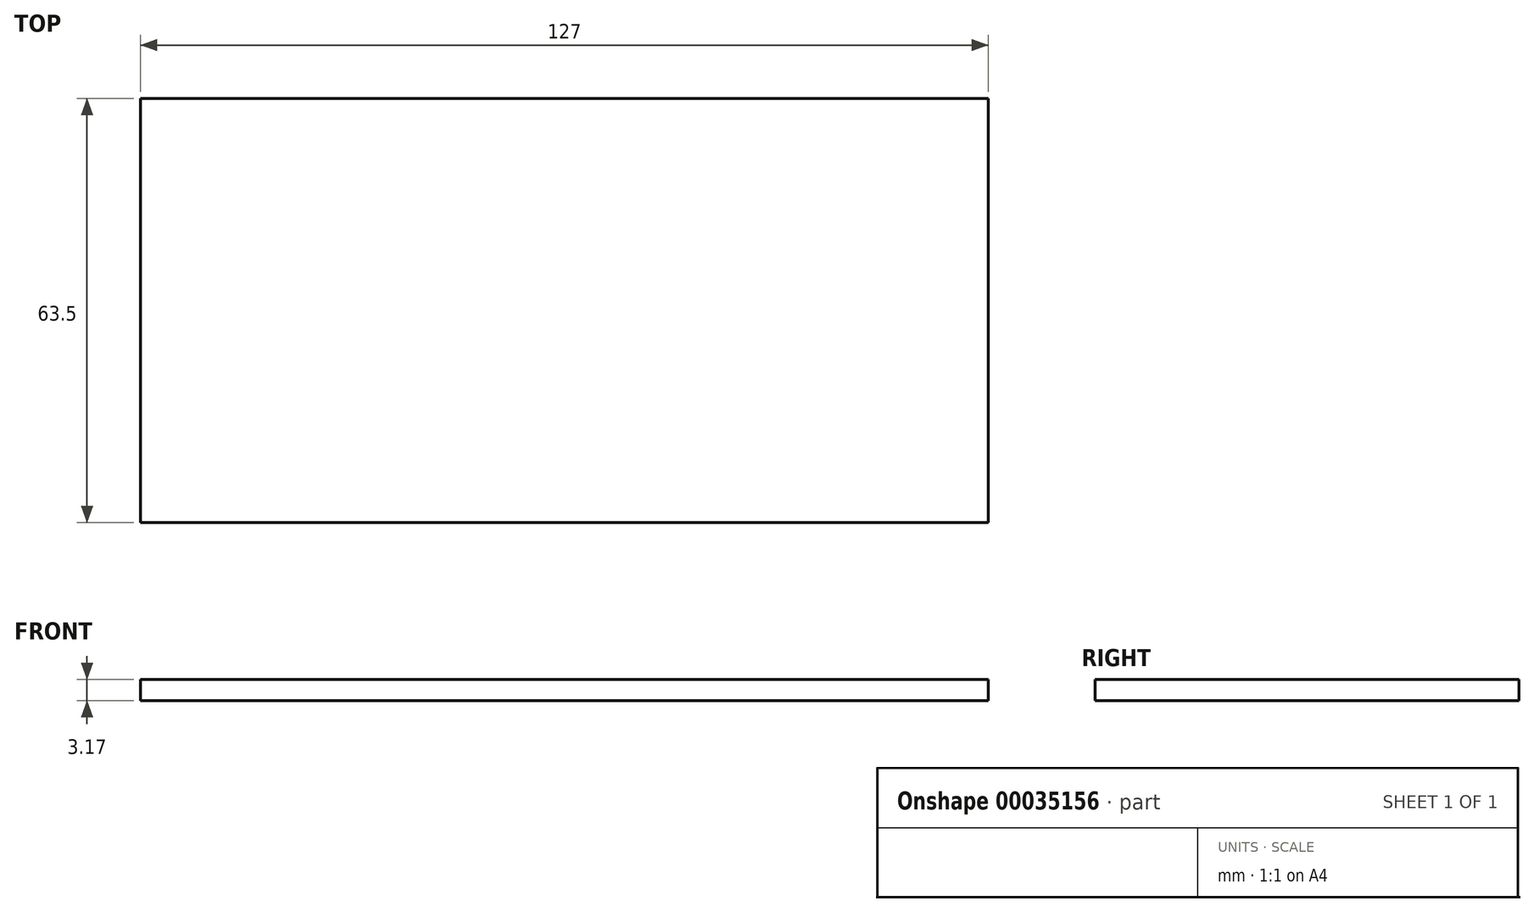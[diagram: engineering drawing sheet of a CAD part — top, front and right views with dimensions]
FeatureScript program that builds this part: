
annotation { "Feature Type Name" : "Feature", "Feature Type Description" : "" }
export const myFeature = defineFeature(function(context is Context, id is Id, definition is map)
    precondition{}
    {
        {
            var Q0;
            Q0=qCreatedBy(makeId("Top.planeOp"),FACE);
            var sketch = newSketch(context, id + "F0", { "sketchPlane" : qUnion([Q0])});
            skLineSegment(sketch, "E0.rect.bottom", {"start": v(63.5, 31.75) * mm, "end": v(-63.5, 31.75) * mm});
            skLineSegment(sketch, "E0.rect.top", {"start": v(63.5, -31.75) * mm, "end": v(-63.5, -31.75) * mm});
            skLineSegment(sketch, "E0.rect.left", {"start": v(63.5, 31.75) * mm, "end": v(63.5, -31.75) * mm});
            skLineSegment(sketch, "E0.rect.right", {"start": v(-63.5, 31.75) * mm, "end": v(-63.5, -31.75) * mm});
            skPoint(sketch, "E0.rect.middle", {"position": v(0, 0) * mm});
            skSolve(sketch);
        }
        {
            var Q0;
            Q0=makeQuery(id+"F0.imprint","IMPRINT",FACE,{"disambiguationData":[TD([[makeQuery(id+"F0.imprint","IMPRINT",EDGE,{"derivedFrom":sQuery(id+"F0.wireOp",EDGE,"E0.rect.bottom")}),1.0]])]});
            extrude(context, id + "F1", {"entities" : qUnion([Q0]), "depth" : 3.17 * mm});
        }
    });
